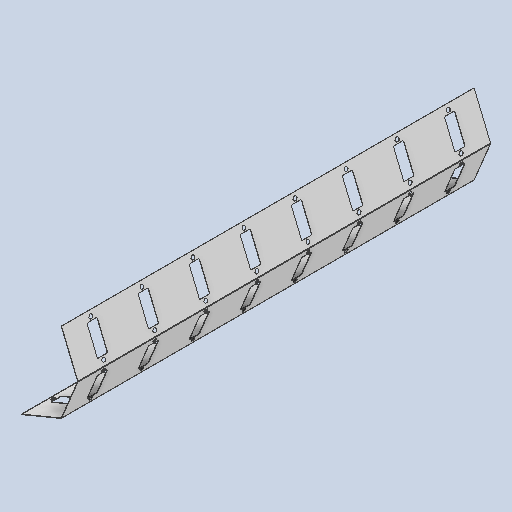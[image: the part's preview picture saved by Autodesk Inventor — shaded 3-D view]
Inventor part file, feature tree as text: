
AUTODESK INVENTOR PART (.ipt)
format: ipt  version: 2025 (Build 290162010, 162A)  size: 924,160 bytes
history: native  units: mm
features: sheet_metal_op x3, other x3, sketch x2, extrude x1, fillet x1, pattern_circular x1, pattern_linear x1
ambient origin geometry x8: Origin, YZ Plane, XZ Plane, XY Plane, X Axis, Y Axis, Z Axis, Center Point
bodies: Body1 (feature_tree)
feature tree (12):
  sheet_metal_op  "Contour Flange2"
  extrude  "Extrusion4"  Depth=2.0mm
  fillet  "Fillet1"  Radius=1.0mm
  pattern_circular  "Circular Pattern1"  [2 undecoded]
  pattern_linear  "Rectangular Pattern2"  Count1=202  [1 undecoded]
  other  "Corner Chamfer1"
  sketch  "Sketch2"  dims[d25=2.0mm d26=2.0mm d27=1.0mm]
  other  "Plate2"
  sheet_metal_op  "Bend2"
  sheet_metal_op  "Corner2"
  sketch  "Sketch10"  dims[d28=4.0mm d29=2.0mm d30=2020.0mm d31=2.0mm d32=3.0mm d33=8.0mm d34=2.0mm d35=2.0mm d56=513.0mm d58=4.0mm d69=0.9mm d70=4.0mm d71=0.9mm d107=135.0mm d108=50.0mm d112=0.0mm d113=0.0mm d114=5.0mm d115=30.0mm d116=90.0deg d118=125.0mm d119=80.0mm d121=250.0mm d122=2.0mm d123=6.0mm d124=45.0deg d125=165.0mm d126=16.8mm d127=16.8mm]
  other  "Definition1"
note: 3 required parameter values undecoded (feature->parameter linkage not recoverable at this tier; creation-order binding heuristic only, values carry confidence <= 0.55)
